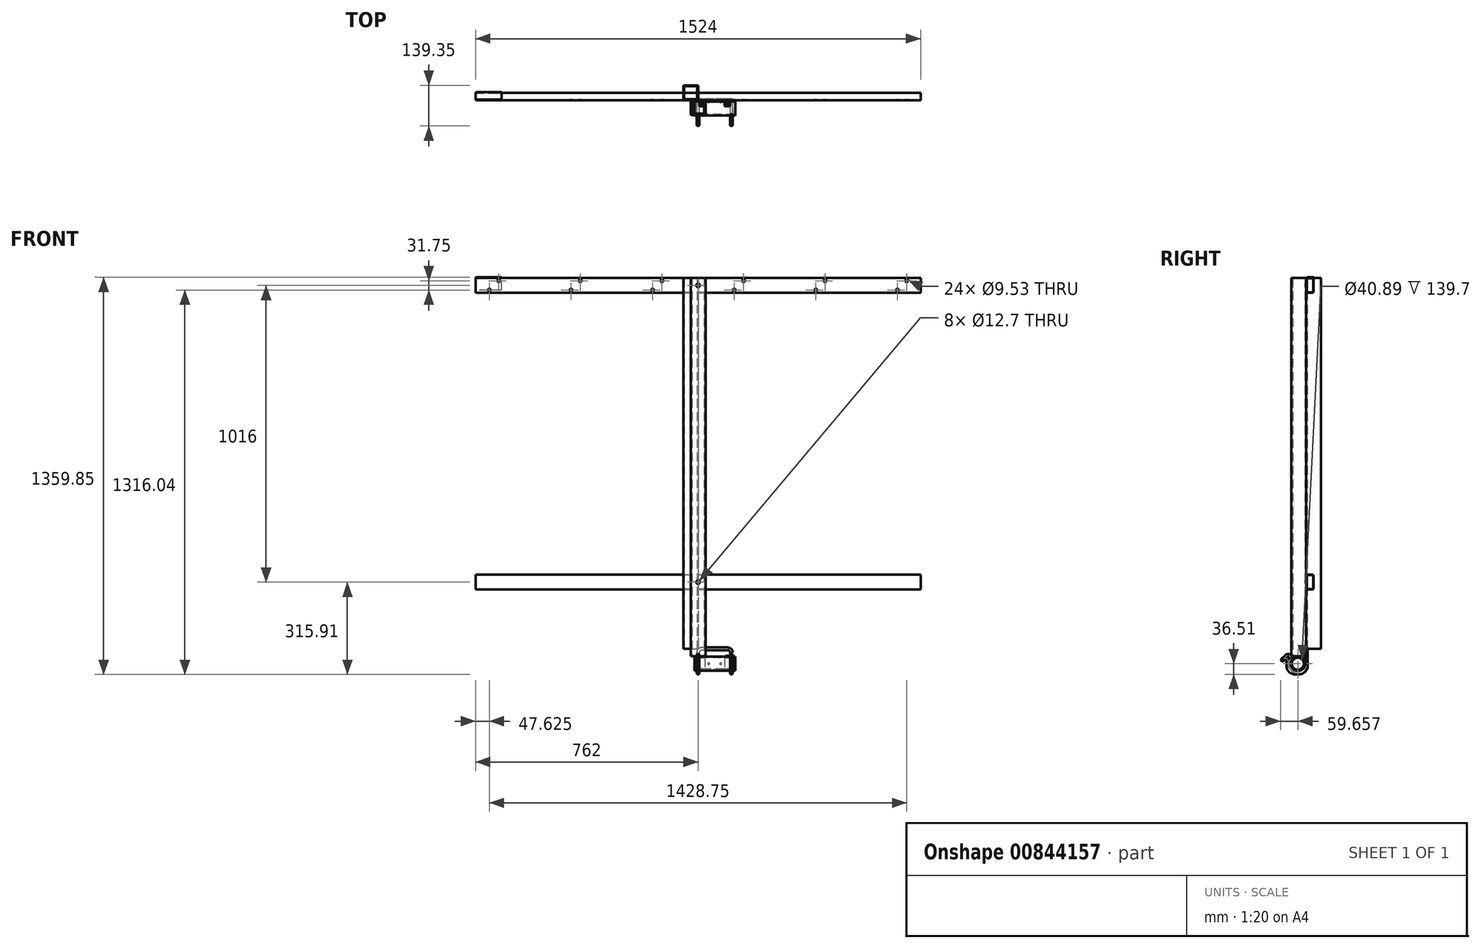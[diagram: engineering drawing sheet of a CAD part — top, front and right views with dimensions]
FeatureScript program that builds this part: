
annotation { "Feature Type Name" : "Feature", "Feature Type Description" : "" }
export const myFeature = defineFeature(function(context is Context, id is Id, definition is map)
    precondition{}
    {
        {
            var Q0;
            Q0=qCreatedBy(makeId("Top.planeOp"),FACE);
            cPlane(context, id + "F0", {"entities" : qUnion([Q0]), "cplaneType" : CPlaneType.OFFSET, "offset" : 457.2 * mm, "oppositeDirection" : true, "width" : 152.4 * mm, "height" : 152.4 * mm});
        }
        {
            var Q0;
            Q0=qCreatedBy(makeId("Front.planeOp"),FACE);
            var sketch = newSketch(context, id + "F1", { "sketchPlane" : qUnion([Q0])});
            skCircle(sketch, "E0.cCircle", {"center": v(0, 0) * mm, "radius": 25.4 * mm, "construction": true});
            skLineSegment(sketch, "E0.0", {"start": v(-25.4, -25.4) * mm, "end": v(-25.4, 25.4) * mm});
            skLineSegment(sketch, "E0.1", {"start": v(-25.4, 25.4) * mm, "end": v(25.4, 25.4) * mm});
            skLineSegment(sketch, "E0.2", {"start": v(25.4, 25.4) * mm, "end": v(25.4, -25.4) * mm});
            skLineSegment(sketch, "E0.3", {"start": v(25.4, -25.4) * mm, "end": v(-25.4, -25.4) * mm});
            skPoint(sketch, "E0.0.midPoint", {"position": v(-25.4, 0) * mm});
            skSolve(sketch);
        }
        {
            var Q0;
            Q0=qCreatedBy(makeId("Right.planeOp"),FACE);
            var sketch = newSketch(context, id + "F2", { "sketchPlane" : qUnion([Q0])});
            skCircle(sketch, "E1", {"center": v(-543.84, -137.57) * mm, "radius": 368.3 * mm, "construction": true});
            skLineSegment(sketch, "E2", {"start": v(-519.16, -505.04) * mm, "end": v(1678.67, -357.4) * mm, "construction": true});
            skCircle(sketch, "E3", {"center": v(613.45, -59.82) * mm, "radius": 368.3 * mm, "construction": true});
            skLineSegment(sketch, "E4", {"start": v(-327.65, 542.52) * mm, "end": v(-154.24, 174.4) * mm, "construction": true});
            skLineSegment(sketch, "E5", {"start": v(-543.84, -137.57) * mm, "end": v(16.21, -99.94) * mm, "construction": true});
            skLineSegment(sketch, "E6", {"start": v(16.21, -99.94) * mm, "end": v(324.48, 435.04) * mm, "construction": true});
            skLineSegment(sketch, "E7", {"start": v(280.4, 522.43) * mm, "end": v(566.34, -44.62) * mm, "construction": true});
            skLineSegment(sketch, "E8", {"start": v(-485.82, 531.9) * mm, "end": v(-227.77, 549.23) * mm, "construction": true});
            skCircle(sketch, "E9", {"center": v(613.45, -59.82) * mm, "radius": 101.6 * mm, "construction": true});
            skCircle(sketch, "E10", {"center": v(-543.84, -137.57) * mm, "radius": 88.9 * mm, "construction": true});
            skLineSegment(sketch, "E11", {"start": v(280.4, 522.43) * mm, "end": v(-543.84, -137.57) * mm, "construction": true});
            skLineSegment(sketch, "E12", {"start": v(-235.61, 347.14) * mm, "end": v(21.55, 315.16) * mm, "construction": true});
            skLineSegment(sketch, "E13", {"start": v(280.4, 522.43) * mm, "end": v(-659.31, 212.17) * mm, "construction": true});
            skSolve(sketch);
        }
        {
            var Q0;
            Q0=qCreatedBy(makeId("Front.planeOp"),FACE);
            var sketch = newSketch(context, id + "F3", { "sketchPlane" : qUnion([Q0])});
            skLineSegment(sketch, "E14.bottom", {"start": v(-762, 1270) * mm, "end": v(762, 1270) * mm});
            skLineSegment(sketch, "E14.top", {"start": v(-762, 1219.2) * mm, "end": v(762, 1219.2) * mm});
            skLineSegment(sketch, "E14.left", {"start": v(-762, 1270) * mm, "end": v(-762, 1219.2) * mm});
            skLineSegment(sketch, "E14.right", {"start": v(762, 1270) * mm, "end": v(762, 1219.2) * mm});
            skPoint(sketch, "E15", {"position": v(0, 1219.2) * mm});
            skLineSegment(sketch, "E16", {"start": v(-484.85, -460.8) * mm, "end": v(945.74, -460.8) * mm, "construction": true});
            skLineSegment(sketch, "E17", {"start": v(433.58, 979.68) * mm, "end": v(963.42, 1509.52) * mm, "construction": true});
            skPoint(sketch, "E18", {"position": v(698.5, 1244.6) * mm});
            skPoint(sketch, "E19", {"position": v(762, 1244.6) * mm});
            skLineSegment(sketch, "E20", {"start": v(0, 1219.2) * mm, "end": v(0, 0) * mm, "construction": true});
            skLineSegment(sketch, "E21.0", {"start": v(-762, 1260.47) * mm, "end": v(762, 1260.48) * mm, "construction": true});
            skLineSegment(sketch, "E22.0", {"start": v(-762, 1228.72) * mm, "end": v(762, 1228.73) * mm, "construction": true});
            skPoint(sketch, "E23", {"position": v(714.38, 1260.48) * mm});
            skPoint(sketch, "E24", {"position": v(682.63, 1228.73) * mm});
            skCircle(sketch, "E25", {"center": v(682.63, 1228.73) * mm, "radius": 4.76 * mm});
            skCircle(sketch, "E26", {"center": v(714.38, 1260.48) * mm, "radius": 4.76 * mm});
            skLineSegment(sketch, "E27.1.0.0", {"start": v(154.18, 979.68) * mm, "end": v(684.02, 1509.52) * mm, "construction": true});
            skLineSegment(sketch, "E27.2.0.0", {"start": v(-125.22, 979.68) * mm, "end": v(404.62, 1509.52) * mm, "construction": true});
            skLineSegment(sketch, "E27.3.0.0", {"start": v(-404.62, 979.68) * mm, "end": v(125.22, 1509.52) * mm, "construction": true});
            skLineSegment(sketch, "E27.4.0.0", {"start": v(-684.02, 979.68) * mm, "end": v(-154.18, 1509.52) * mm, "construction": true});
            skLineSegment(sketch, "E27.5.0.0", {"start": v(-963.42, 979.68) * mm, "end": v(-433.58, 1509.52) * mm, "construction": true});
            skLineSegment(sketch, "E27.direction1", {"start": v(433.58, 979.68) * mm, "end": v(154.18, 979.68) * mm, "construction": true});
            skLineSegment(sketch, "E28.bottom", {"start": v(-762, 203.2) * mm, "end": v(762, 203.2) * mm});
            skLineSegment(sketch, "E28.top", {"start": v(-762, 254) * mm, "end": v(762, 254) * mm});
            skLineSegment(sketch, "E28.left", {"start": v(-762, 203.2) * mm, "end": v(-762, 254) * mm});
            skLineSegment(sketch, "E28.right", {"start": v(762, 203.2) * mm, "end": v(762, 254) * mm});
            skLineSegment(sketch, "E29", {"start": v(762, 1244.6) * mm, "end": v(-762, 1244.6) * mm, "construction": true});
            skPoint(sketch, "E30", {"position": v(762, 228.6) * mm});
            skLineSegment(sketch, "E31", {"start": v(438.07, 1505.03) * mm, "end": v(698.5, 1244.6) * mm, "construction": true});
            skSolve(sketch);
        }
        {
            var Q0;
            Q0=sQuery(id+"F3.wireOp",EDGE,"E29");
            cPoint(context, id + "F4", {"entities" : qUnion([Q0]), "parameter" : 0.5});
        }
        {
            var Q0;
            Q0 = qCreatedBy(id + "F4" ,VERTEX);
            var Q1;
            Q1=sQuery(id+"F3.wireOp",EDGE,"E20");
            cPlane(context, id + "F5", {"entities" : qUnion([Q0, Q1]), "cplaneType" : CPlaneType.LINE_POINT, "offset" : 25.4 * mm, "width" : 152.4 * mm, "height" : 152.4 * mm});
        }
        {
            var Q0;
            Q0=qCreatedBy(makeId("Front.planeOp"),FACE);
            var sketch = newSketch(context, id + "F6", { "sketchPlane" : qUnion([Q0])});
            skLineSegment(sketch, "E32.bottom", {"start": v(-25.4, 1270) * mm, "end": v(25.4, 1270) * mm});
            skLineSegment(sketch, "E32.top", {"start": v(-25.4, 0) * mm, "end": v(25.4, 0) * mm});
            skLineSegment(sketch, "E32.left", {"start": v(-25.4, 1270) * mm, "end": v(-25.4, 0) * mm});
            skLineSegment(sketch, "E32.right", {"start": v(25.4, 1270) * mm, "end": v(25.4, 0) * mm});
            skPoint(sketch, "E33", {"position": v(0, 0) * mm});
            skLineSegment(sketch, "E34", {"start": v(301.3, 736.6) * mm, "end": v(-528.15, 736.6) * mm, "construction": true});
            skSolve(sketch);
        }
        {
            var Q0;
            Q0=qCreatedBy(makeId("Front.planeOp"),FACE);
            var sketch = newSketch(context, id + "F7", { "sketchPlane" : qUnion([Q0])});
            skLineSegment(sketch, "E35", {"start": v(381, 1244.6) * mm, "end": v(0, 863.6) * mm, "construction": true});
            skLineSegment(sketch, "E36", {"start": v(0, 482.6) * mm, "end": v(254, 228.6) * mm, "construction": true});
            skLineSegment(sketch, "E37", {"start": v(762, 228.6) * mm, "end": v(-497.78, 228.6) * mm, "construction": true});
            skSolve(sketch);
        }
        {
            var Q0;
            Q0=qCreatedBy(makeId("Front.planeOp"),FACE);
            var sketch = newSketch(context, id + "F8", { "sketchPlane" : qUnion([Q0])});
            skLineSegment(sketch, "E38.bottom", {"start": v(-25.4, 1270) * mm, "end": v(25.4, 1270) * mm});
            skLineSegment(sketch, "E38.top", {"start": v(-25.4, -25.4) * mm, "end": v(25.4, -25.4) * mm});
            skLineSegment(sketch, "E38.left", {"start": v(-25.4, 1270) * mm, "end": v(-25.4, -25.4) * mm});
            skLineSegment(sketch, "E38.right", {"start": v(25.4, 1270) * mm, "end": v(25.4, -25.4) * mm});
            skSolve(sketch);
        }
        {
            var Q0;
            Q0 = qSketchRegion(id + "F8", true);
            extrude(context, id + "F9", {"entities" : qUnion([Q0]), "depth" : 50.8 * mm, "offsetDistance" : 25.4 * mm});
        }
        {
            var Q0;
            Q0=makeQuery(id+"F9.opExtrude","SWEPT_FACE",FACE,{"disambiguationData":[OSD([sQuery(id+"F8.wireOp",EDGE,"E38.bottom")])]});
            var Q1;
            Q1=makeQuery(id+"F9.opExtrude","SWEPT_FACE",FACE,{"disambiguationData":[OSD([sQuery(id+"F8.wireOp",EDGE,"E38.top")])]});
            shell(context, id + "F10", {"entities" : qUnion([Q0, Q1]), "thickness" : 4.78 * mm});
        }
        {
            var Q0;
            Q0=qCreatedBy(makeId("Front.planeOp"),FACE);
            var sketch = newSketch(context, id + "F11", { "sketchPlane" : qUnion([Q0])});
            skLineSegment(sketch, "E39.bottom", {"start": v(-762, 1270) * mm, "end": v(762, 1270) * mm});
            skLineSegment(sketch, "E39.top", {"start": v(-762, 1219.2) * mm, "end": v(762, 1219.2) * mm});
            skLineSegment(sketch, "E39.left", {"start": v(-762, 1270) * mm, "end": v(-762, 1219.2) * mm});
            skLineSegment(sketch, "E39.right", {"start": v(762, 1270) * mm, "end": v(762, 1219.2) * mm});
            skSolve(sketch);
        }
        {
            var Q0;
            Q0 = qSketchRegion(id + "F11", true);
            extrude(context, id + "F12", {"entities" : qUnion([Q0]), "oppositeDirection" : true, "depth" : 25.4 * mm, "offsetDistance" : 25.4 * mm});
        }
        {
            var Q0;
            Q0=makeQuery(id+"F12.opExtrude","CAP_EDGE",EDGE,{"disambiguationData":[OSD([sQuery(id+"F11.wireOp",EDGE,"E39.bottom")])],"isStart":true});
            var Q1;
            Q1=makeQuery(id+"F12.opExtrude","CAP_EDGE",EDGE,{"disambiguationData":[OSD([sQuery(id+"F11.wireOp",EDGE,"E39.top")])],"isStart":true});
            var Q2;
            Q2=makeQuery(id+"F12.opExtrude","CAP_EDGE",EDGE,{"disambiguationData":[OSD([sQuery(id+"F11.wireOp",EDGE,"E39.bottom")])],"isStart":false});
            var Q3;
            Q3=makeQuery(id+"F12.opExtrude","CAP_EDGE",EDGE,{"disambiguationData":[OSD([sQuery(id+"F11.wireOp",EDGE,"E39.top")])],"isStart":false});
            fillet(context, id + "F13", {"entities" : qUnion([Q0, Q1, Q2, Q3]), "radius" : 5.08 * mm, "tangentPropagation" : true, "allowEdgeOverflow" : false});
        }
        {
            var Q0;
            Q0=makeQuery(id+"F12.opExtrude","SWEPT_FACE",FACE,{"disambiguationData":[OSD([sQuery(id+"F11.wireOp",EDGE,"E39.right")])]});
            var Q1;
            Q1=makeQuery(id+"F12.opExtrude","SWEPT_FACE",FACE,{"disambiguationData":[OSD([sQuery(id+"F11.wireOp",EDGE,"E39.left")])]});
            shell(context, id + "F14", {"entities" : qUnion([Q0, Q1]), "thickness" : 1.6 * mm});
        }
        {
            var Q0;
            Q0=makeQuery(id+"F3.imprint","IMPRINT",FACE,{"disambiguationData":[TD([[makeQuery(id+"F3.imprint","IMPRINT",EDGE,{"derivedFrom":sQuery(id+"F3.wireOp",EDGE,"E14.bottom")}),-1.0]])]});
            var sketch = newSketch(context, id + "F15", { "sketchPlane" : qUnion([Q0])});
            skCircle(sketch, "E40", {"center": v(714.38, 1260.48) * mm, "radius": 4.76 * mm});
            skCircle(sketch, "E41", {"center": v(682.63, 1228.73) * mm, "radius": 4.76 * mm});
            skCircle(sketch, "E42.1.0.0", {"center": v(434.98, 1260.48) * mm, "radius": 4.76 * mm});
            skCircle(sketch, "E42.1.0.1", {"center": v(403.23, 1228.73) * mm, "radius": 4.76 * mm});
            skCircle(sketch, "E42.2.0.0", {"center": v(155.58, 1260.48) * mm, "radius": 4.76 * mm});
            skCircle(sketch, "E42.2.0.1", {"center": v(123.83, 1228.73) * mm, "radius": 4.76 * mm});
            skCircle(sketch, "E42.3.0.0", {"center": v(-123.82, 1260.48) * mm, "radius": 4.76 * mm});
            skCircle(sketch, "E42.3.0.1", {"center": v(-155.57, 1228.73) * mm, "radius": 4.76 * mm});
            skCircle(sketch, "E42.4.0.0", {"center": v(-403.22, 1260.47) * mm, "radius": 4.76 * mm});
            skCircle(sketch, "E42.4.0.1", {"center": v(-434.97, 1228.73) * mm, "radius": 4.76 * mm});
            skCircle(sketch, "E42.5.0.0", {"center": v(-682.62, 1260.47) * mm, "radius": 4.76 * mm});
            skCircle(sketch, "E42.5.0.1", {"center": v(-714.37, 1228.73) * mm, "radius": 4.76 * mm});
            skLineSegment(sketch, "E42.direction1", {"start": v(714.38, 1260.48) * mm, "end": v(434.98, 1260.48) * mm, "construction": true});
            skSolve(sketch);
        }
        {
            var Q0;
            Q0 = qSketchRegion(id + "F15", true);
            extrude(context, id + "F16", {"entities" : qUnion([Q0]), "operationType" : NewBodyOperationType.REMOVE, "oppositeDirection" : true, "depth" : 25.4 * mm, "offsetDistance" : 25.4 * mm});
        }
        {
            var Q0;
            Q0=qCreatedBy(makeId("Front.planeOp"),FACE);
            var sketch = newSketch(context, id + "F17", { "sketchPlane" : qUnion([Q0])});
            skLineSegment(sketch, "E43.bottom", {"start": v(-762, 254) * mm, "end": v(762, 254) * mm});
            skLineSegment(sketch, "E43.top", {"start": v(-762, 203.2) * mm, "end": v(762, 203.2) * mm});
            skLineSegment(sketch, "E43.left", {"start": v(-762, 254) * mm, "end": v(-762, 203.2) * mm});
            skLineSegment(sketch, "E43.right", {"start": v(762, 254) * mm, "end": v(762, 203.2) * mm});
            skSolve(sketch);
        }
        {
            var Q0;
            Q0 = qSketchRegion(id + "F17", true);
            extrude(context, id + "F18", {"entities" : qUnion([Q0]), "oppositeDirection" : true, "depth" : 25.4 * mm, "offsetDistance" : 25.4 * mm});
        }
        {
            var Q0;
            Q0=makeQuery(id+"F18.opExtrude","CAP_EDGE",EDGE,{"disambiguationData":[OSD([sQuery(id+"F17.wireOp",EDGE,"E43.bottom")])],"isStart":true});
            var Q1;
            Q1=makeQuery(id+"F18.opExtrude","CAP_EDGE",EDGE,{"disambiguationData":[OSD([sQuery(id+"F17.wireOp",EDGE,"E43.bottom")])],"isStart":false});
            var Q2;
            Q2=makeQuery(id+"F18.opExtrude","CAP_EDGE",EDGE,{"disambiguationData":[OSD([sQuery(id+"F17.wireOp",EDGE,"E43.top")])],"isStart":true});
            var Q3;
            Q3=makeQuery(id+"F18.opExtrude","CAP_EDGE",EDGE,{"disambiguationData":[OSD([sQuery(id+"F17.wireOp",EDGE,"E43.top")])],"isStart":false});
            fillet(context, id + "F19", {"entities" : qUnion([Q0, Q1, Q2, Q3]), "radius" : 5.08 * mm, "tangentPropagation" : true, "allowEdgeOverflow" : false});
        }
        {
            var Q0;
            Q0=makeQuery(id+"F18.opExtrude","SWEPT_FACE",FACE,{"disambiguationData":[OSD([sQuery(id+"F17.wireOp",EDGE,"E43.right")])]});
            var Q1;
            Q1=makeQuery(id+"F18.opExtrude","SWEPT_FACE",FACE,{"disambiguationData":[OSD([sQuery(id+"F17.wireOp",EDGE,"E43.left")])]});
            shell(context, id + "F20", {"entities" : qUnion([Q0, Q1]), "thickness" : 1.6 * mm});
        }
        {
            var Q0;
            Q0=makeQuery(id+"F12.opExtrude","SWEPT_FACE",FACE,{"disambiguationData":[OSD([sQuery(id+"F11.wireOp",EDGE,"E39.left")])]});
            var sketch = newSketch(context, id + "F21", { "sketchPlane" : qUnion([Q0])});
            skLineSegment(sketch, "E44", {"start": v(-2.54, 1270) * mm, "end": v(-22.86, 1270) * mm});
            skLineSegment(sketch, "E45", {"start": v(-25.4, 1267.46) * mm, "end": v(-25.4, 1228.09) * mm});
            skLineSegment(sketch, "E46", {"start": v(-25.4, 1228.09) * mm, "end": v(-27.94, 1228.09) * mm});
            skLineSegment(sketch, "E47", {"start": v(-27.94, 1228.09) * mm, "end": v(-27.94, 1267.46) * mm});
            skLineSegment(sketch, "E48", {"start": v(-22.86, 1272.54) * mm, "end": v(-2.54, 1272.54) * mm});
            skLineSegment(sketch, "E49", {"start": v(-2.54, 1272.54) * mm, "end": v(-2.54, 1270) * mm});
            skPoint(sketch, "E50.visualSharp", {"position": v(-25.4, 1270) * mm});
            skArc(sketch, "E50.filletArc", {"start": v(-22.86, 1270) * mm, "mid": v(-24.66, 1269.26) * mm, "end": v(-25.4, 1267.46) * mm});
            skPoint(sketch, "E51.visualSharp", {"position": v(-27.94, 1272.54) * mm});
            skArc(sketch, "E51.filletArc", {"start": v(-22.86, 1272.54) * mm, "mid": v(-26.45, 1271.05) * mm, "end": v(-27.94, 1267.46) * mm});
            skSolve(sketch);
        }
        {
            var Q0;
            Q0 = qSketchRegion(id + "F21", true);
            extrude(context, id + "F22", {"entities" : qUnion([Q0]), "oppositeDirection" : true, "depth" : 88.9 * mm, "offsetDistance" : 25.4 * mm});
        }
        {
            var Q0;
            Q0=makeQuery(id+"F22.opExtrude","CAP_FACE",FACE,{"disambiguationData":[OSD([sQuery(id+"F21.wireOp",EDGE,"E44"),sQuery(id+"F21.wireOp",EDGE,"E45"),sQuery(id+"F21.wireOp",EDGE,"E46"),sQuery(id+"F21.wireOp",EDGE,"E47"),sQuery(id+"F21.wireOp",EDGE,"E48"),sQuery(id+"F21.wireOp",EDGE,"E49"),sQuery(id+"F21.wireOp",EDGE,"E50.filletArc"),sQuery(id+"F21.wireOp",EDGE,"E51.filletArc")])],"isStart":true});
            cPlane(context, id + "F23", {"entities" : qUnion([Q0]), "cplaneType" : CPlaneType.OFFSET, "offset" : 6.35 * mm, "oppositeDirection" : true, "width" : 152.4 * mm, "height" : 152.4 * mm});
        }
        {
            var Q0;
            Q0=qCreatedBy(id+"F23.planeOp",FACE);
            var sketch = newSketch(context, id + "F24", { "sketchPlane" : qUnion([Q0])});
            skLineSegment(sketch, "E52", {"start": v(-32.7, 1270) * mm, "end": v(-32.7, 1244.6) * mm});
            skArc(sketch, "E53", {"start": v(-96.2, 1244.6) * mm, "mid": v(-64.45, 1212.85) * mm, "end": v(-32.7, 1244.6) * mm});
            skLineSegment(sketch, "E54", {"start": v(-96.2, 1244.6) * mm, "end": v(-96.2, 1262.1) * mm});
            skLineSegment(sketch, "E55", {"start": v(-101.78, 1275.58) * mm, "end": v(-105.18, 1278.98) * mm});
            skPoint(sketch, "E56.visualSharp", {"position": v(-96.2, 1270) * mm});
            skArc(sketch, "E56.filletArc", {"start": v(-96.2, 1262.1) * mm, "mid": v(-97.65, 1269.4) * mm, "end": v(-101.78, 1275.58) * mm});
            skSolve(sketch);
        }
        {
            var Q0;
            Q0=makeQuery(id+"F22.opExtrude","CAP_FACE",FACE,{"disambiguationData":[OSD([sQuery(id+"F21.wireOp",EDGE,"E44"),sQuery(id+"F21.wireOp",EDGE,"E45"),sQuery(id+"F21.wireOp",EDGE,"E46"),sQuery(id+"F21.wireOp",EDGE,"E47"),sQuery(id+"F21.wireOp",EDGE,"E48"),sQuery(id+"F21.wireOp",EDGE,"E49"),sQuery(id+"F21.wireOp",EDGE,"E50.filletArc"),sQuery(id+"F21.wireOp",EDGE,"E51.filletArc")])],"isStart":false});
            cPlane(context, id + "F25", {"entities" : qUnion([Q0]), "cplaneType" : CPlaneType.OFFSET, "offset" : 6.35 * mm, "oppositeDirection" : true, "width" : 152.4 * mm, "height" : 152.4 * mm});
        }
        {
            var Q0;
            Q0=qCreatedBy(id+"F25.planeOp",FACE);
            var sketch = newSketch(context, id + "F26", { "sketchPlane" : qUnion([Q0])});
            skLineSegment(sketch, "E57", {"start": v(32.7, 1270) * mm, "end": v(32.7, 1168.4) * mm});
            skLineSegment(sketch, "E58", {"start": v(96.2, 1168.4) * mm, "end": v(96.2, 1185.9) * mm});
            skLineSegment(sketch, "E59", {"start": v(101.78, 1199.38) * mm, "end": v(114.16, 1211.76) * mm});
            skArc(sketch, "E60", {"start": v(32.7, 1168.4) * mm, "mid": v(64.45, 1136.65) * mm, "end": v(96.2, 1168.4) * mm});
            skPoint(sketch, "E61.visualSharp", {"position": v(96.2, 1193.8) * mm});
            skArc(sketch, "E61.filletArc", {"start": v(101.78, 1199.38) * mm, "mid": v(97.65, 1193.2) * mm, "end": v(96.2, 1185.9) * mm});
            skSolve(sketch);
        }
        {
            var Q0;
            Q0=sQuery(id+"F26.wireOp",VERTEX,"E57.start");
            var Q1;
            Q1=sQuery(id+"F26.wireOp",EDGE,"E57");
            cPlane(context, id + "F27", {"entities" : qUnion([Q0, Q1]), "cplaneType" : CPlaneType.LINE_POINT, "offset" : 25.4 * mm, "width" : 152.4 * mm, "height" : 152.4 * mm});
        }
        {
            var Q0;
            Q0=qCreatedBy(id+"F27.planeOp",FACE);
            var sketch = newSketch(context, id + "F28", { "sketchPlane" : qUnion([Q0])});
            skCircle(sketch, "E62", {"center": v(-679.45, -32.7) * mm, "radius": 4.76 * mm});
            skSolve(sketch);
        }
        {
            var Q0;
            Q0=makeQuery(id+"F28.imprint","IMPRINT",FACE,{"disambiguationData":[TD([[makeQuery(id+"F28.imprint","IMPRINT",EDGE,{"derivedFrom":sQuery(id+"F28.wireOp",EDGE,"E62")}),1.0]])]});
            var Q1;
            Q1 = qConstructionFilter(qBodyType(qCreatedBy(id + "F26" ,EDGE), BodyType.WIRE), ConstructionObject.NO);
            sweep(context, id + "F29", {"profiles" : qUnion([Q0]), "path" : qUnion([Q1])});
        }
        {
            var Q0;
            Q0=qCreatedBy(id+"F27.planeOp",FACE);
            var sketch = newSketch(context, id + "F30", { "sketchPlane" : qUnion([Q0])});
            skCircle(sketch, "E63", {"center": v(-755.65, -32.7) * mm, "radius": 4.76 * mm});
            skSolve(sketch);
        }
        {
            var Q0;
            Q0=makeQuery(id+"F30.imprint","IMPRINT",FACE,{"disambiguationData":[TD([[makeQuery(id+"F30.imprint","IMPRINT",EDGE,{"derivedFrom":sQuery(id+"F30.wireOp",EDGE,"E63")}),1.0]])]});
            var Q1;
            Q1=sQuery(id+"F30.wireOp",EDGE,"E63");
            var Q2;
            Q2 = qConstructionFilter(qBodyType(qCreatedBy(id + "F24" ,EDGE), BodyType.WIRE), ConstructionObject.NO);
            sweep(context, id + "F31", {"profiles" : qUnion([Q0]), "surfaceProfiles" : qUnion([Q1]), "path" : qUnion([Q2])});
        }
        {
            var Q0;
            Q0=sQuery(id+"F24.wireOp",VERTEX,"E53.center");
            var Q1;
            Q1=makeQuery(id+"F22.opExtrude","CAP_EDGE",EDGE,{"disambiguationData":[OSD([sQuery(id+"F21.wireOp",EDGE,"E48")])],"isStart":true});
            cPlane(context, id + "F32", {"entities" : qUnion([Q0, Q1]), "cplaneType" : CPlaneType.LINE_POINT, "offset" : 25.4 * mm, "oppositeDirection" : true, "width" : 152.4 * mm, "height" : 152.4 * mm});
        }
        {
            var Q0;
            Q0=qCreatedBy(id+"F25.planeOp",FACE);
            var sketch = newSketch(context, id + "F33", { "sketchPlane" : qUnion([Q0])});
            skLineSegment(sketch, "E64", {"start": v(32.7, 1270) * mm, "end": v(32.7, 1219.2) * mm});
            skLineSegment(sketch, "E65", {"start": v(96.2, 1162.05) * mm, "end": v(96.2, 1187.45) * mm});
            skArc(sketch, "E66", {"start": v(46, 1156.54) * mm, "mid": v(73.57, 1136.8) * mm, "end": v(96.2, 1162.05) * mm});
            skArc(sketch, "E67", {"start": v(96.2, 1187.45) * mm, "mid": v(104.04, 1199.18) * mm, "end": v(117.88, 1196.43) * mm});
            skPoint(sketch, "E68.orphan", {"position": v(32.7, 1162.05) * mm});
            skPoint(sketch, "E69.visualSharp", {"position": v(32.7, 1181.1) * mm});
            skArc(sketch, "E69.filletArc", {"start": v(32.7, 1219.2) * mm, "mid": v(32.85, 1216.43) * mm, "end": v(33.3, 1213.69) * mm});
            skPoint(sketch, "E70.visualSharp", {"position": v(51.75, 1187.45) * mm});
            skCircle(sketch, "E71", {"center": v(70.8, 1162.05) * mm, "radius": 15.88 * mm, "construction": true});
            skLineSegment(sketch, "E72", {"start": v(55.67, 1136.65) * mm, "end": v(70.8, 1136.65) * mm, "construction": true});
            skPoint(sketch, "E72.startSnap0", {"position": v(70.8, 1136.65) * mm});
            skLineSegment(sketch, "E73", {"start": v(108.9, 1187.45) * mm, "end": v(117.88, 1196.43) * mm, "construction": true});
            skLineSegment(sketch, "E74", {"start": v(46, 1156.54) * mm, "end": v(33.3, 1213.69) * mm});
            skPoint(sketch, "E75.orphan", {"position": v(45.4, 1162.05) * mm});
            skSolve(sketch);
        }
        {
            var Q0;
            Q0 = qSketchRegion(id + "F28", true);
            var Q1;
            Q1 = qConstructionFilter(qBodyType(qCreatedBy(id + "F33" ,EDGE), BodyType.WIRE), ConstructionObject.NO);
            sweep(context, id + "F34", {"operationType" : NewBodyOperationType.ADD, "profiles" : qUnion([Q0]), "path" : qUnion([Q1])});
        }
        {
            var Q0;
            Q0=qCreatedBy(id+"F23.planeOp",FACE);
            var sketch = newSketch(context, id + "F35", { "sketchPlane" : qUnion([Q0])});
            skLineSegment(sketch, "E76", {"start": v(-32.7, 1270) * mm, "end": v(-32.7, 1244.6) * mm});
            skLineSegment(sketch, "E77", {"start": v(-36.73, 1235.32) * mm, "end": v(-53.46, 1219.69) * mm});
            skLineSegment(sketch, "E78", {"start": v(-96.2, 1238.25) * mm, "end": v(-96.2, 1263.65) * mm});
            skArc(sketch, "E79", {"start": v(-96.2, 1238.25) * mm, "mid": v(-80.92, 1214.95) * mm, "end": v(-53.46, 1219.69) * mm});
            skPoint(sketch, "E80.visualSharp", {"position": v(-32.7, 1239.08) * mm});
            skArc(sketch, "E80.filletArc", {"start": v(-36.73, 1235.32) * mm, "mid": v(-33.75, 1239.54) * mm, "end": v(-32.7, 1244.6) * mm});
            skLineSegment(sketch, "E81", {"start": v(-70.8, 1212.85) * mm, "end": v(11.7, 1212.85) * mm, "construction": true});
            skArc(sketch, "E82", {"start": v(-96.2, 1263.65) * mm, "mid": v(-104.04, 1275.38) * mm, "end": v(-117.88, 1272.63) * mm});
            skLineSegment(sketch, "E83", {"start": v(-108.9, 1263.65) * mm, "end": v(-117.88, 1272.63) * mm, "construction": true});
            skSolve(sketch);
        }
        {
            var Q0;
            Q0 = qSketchRegion(id + "F30", true);
            var Q1;
            Q1 = qConstructionFilter(qBodyType(qCreatedBy(id + "F35" ,EDGE), BodyType.WIRE), ConstructionObject.NO);
            sweep(context, id + "F36", {"operationType" : NewBodyOperationType.ADD, "profiles" : qUnion([Q0]), "path" : qUnion([Q1])});
        }
        {
            var Q0;
            Q0=makeQuery(id+"F34.opSweep","CAP_EDGE",EDGE,{"disambiguationData":[OSD([sQuery(id+"F28.wireOp",EDGE,"E62"),sQuery(id+"F33.wireOp",VERTEX,"E67.end")])],"isStart":false});
            var Q1;
            Q1=makeQuery(id+"F36.opSweep","CAP_EDGE",EDGE,{"disambiguationData":[OSD([sQuery(id+"F30.wireOp",EDGE,"E63"),sQuery(id+"F35.wireOp",VERTEX,"E82.end")])],"isStart":false});
            var Q2;
            Q2=makeQuery(id+"F36.opSweep","CAP_EDGE",EDGE,{"disambiguationData":[OSD([sQuery(id+"F30.wireOp",EDGE,"E63"),sQuery(id+"F35.wireOp",VERTEX,"E76.start")])],"isStart":true});
            var Q3;
            Q3=makeQuery(id+"F34.opSweep","CAP_EDGE",EDGE,{"disambiguationData":[OSD([sQuery(id+"F28.wireOp",EDGE,"E62"),sQuery(id+"F33.wireOp",VERTEX,"E64.start")])],"isStart":true});
            fillet(context, id + "F37", {"entities" : qUnion([Q0, Q1, Q2, Q3]), "radius" : 2.54 * mm, "tangentPropagation" : true, "allowEdgeOverflow" : false});
        }
        {
            var Q0;
            Q0=makeQuery(id+"F12.opExtrude","CAP_FACE",FACE,{"disambiguationData":[OSD([sQuery(id+"F11.wireOp",EDGE,"E39.bottom"),sQuery(id+"F11.wireOp",EDGE,"E39.top"),sQuery(id+"F11.wireOp",EDGE,"E39.left"),sQuery(id+"F11.wireOp",EDGE,"E39.right")])],"isStart":false});
            var sketch = newSketch(context, id + "F38", { "sketchPlane" : qUnion([Q0])});
            skCircle(sketch, "E84", {"center": v(0, 1244.6) * mm, "radius": 6.35 * mm});
            skSolve(sketch);
        }
        {
            var Q0;
            Q0 = qSketchRegion(id + "F38", true);
            extrude(context, id + "F39", {"entities" : qUnion([Q0]), "operationType" : NewBodyOperationType.REMOVE, "endBound" : BoundingType.THROUGH_ALL, "oppositeDirection" : true, "depth" : 25.4 * mm, "offsetDistance" : 25.4 * mm});
        }
        {
            var Q0;
            Q0=makeQuery(id+"F18.opExtrude","CAP_FACE",FACE,{"disambiguationData":[OSD([sQuery(id+"F17.wireOp",EDGE,"E43.bottom"),sQuery(id+"F17.wireOp",EDGE,"E43.top"),sQuery(id+"F17.wireOp",EDGE,"E43.left"),sQuery(id+"F17.wireOp",EDGE,"E43.right")])],"isStart":false});
            var sketch = newSketch(context, id + "F40", { "sketchPlane" : qUnion([Q0])});
            skCircle(sketch, "E85", {"center": v(0, 228.6) * mm, "radius": 6.35 * mm});
            skSolve(sketch);
        }
        {
            var Q0;
            Q0 = qSketchRegion(id + "F40", true);
            extrude(context, id + "F41", {"entities" : qUnion([Q0]), "operationType" : NewBodyOperationType.REMOVE, "endBound" : BoundingType.THROUGH_ALL, "oppositeDirection" : true, "depth" : 25.4 * mm, "offsetDistance" : 25.4 * mm});
        }
        {
            var Q0;
            Q0=qCreatedBy(makeId("Front.planeOp"),FACE);
            var sketch = newSketch(context, id + "F42", { "sketchPlane" : qUnion([Q0])});
            skLineSegment(sketch, "E86", {"start": v(12.7, 0) * mm, "end": v(101.6, 0) * mm});
            skLineSegment(sketch, "E87", {"start": v(0, -12.7) * mm, "end": v(0, -50.8) * mm});
            skLineSegment(sketch, "E88", {"start": v(114.3, -12.7) * mm, "end": v(114.3, -50.8) * mm});
            skPoint(sketch, "E89.visualSharp", {"position": v(0, 0) * mm});
            skArc(sketch, "E89.filletArc", {"start": v(12.7, 0) * mm, "mid": v(3.72, -3.72) * mm, "end": v(0, -12.7) * mm});
            skPoint(sketch, "E90.visualSharp", {"position": v(114.3, 0) * mm});
            skArc(sketch, "E90.filletArc", {"start": v(114.3, -12.7) * mm, "mid": v(110.58, -3.72) * mm, "end": v(101.6, 0) * mm});
            skSolve(sketch);
        }
        {
            var Q0;
            Q0=qCreatedBy(makeId("Right.planeOp"),FACE);
            var sketch = newSketch(context, id + "F43", { "sketchPlane" : qUnion([Q0])});
            skArc(sketch, "E91", {"start": v(-53.91, -36.35) * mm, "mid": v(-36.37, -78.7) * mm, "end": v(0, -50.8) * mm});
            skLineSegment(sketch, "E92", {"start": v(-28.9, -50.8) * mm, "end": v(-53.91, -36.35) * mm, "construction": true});
            skLineSegment(sketch, "E93", {"start": v(-28.9, -50.8) * mm, "end": v(0, -50.8) * mm, "construction": true});
            skArc(sketch, "E94", {"start": v(-53.91, -36.35) * mm, "mid": v(-57.4, -23.34) * mm, "end": v(-70.41, -26.83) * mm});
            skLineSegment(sketch, "E95", {"start": v(-70.41, -26.83) * mm, "end": v(-75.17, -35.08) * mm});
            skSolve(sketch);
        }
        {
            var Q0;
            Q0=qCreatedBy(makeId("Right.planeOp"),FACE);
            var Q1;
            Q1=sQuery(id+"F42.wireOp",VERTEX,"E88.end");
            cPlane(context, id + "F44", {"entities" : qUnion([Q0, Q1]), "cplaneType" : CPlaneType.PLANE_POINT, "offset" : 25.4 * mm, "width" : 152.4 * mm, "height" : 152.4 * mm});
        }
        {
            var Q0;
            Q0=qCreatedBy(id+"F44.planeOp",FACE);
            var sketch = newSketch(context, id + "F45", { "sketchPlane" : qUnion([Q0])});
            skArc(sketch, "E96", {"start": v(-53.91, -36.35) * mm, "mid": v(-36.37, -78.7) * mm, "end": v(0, -50.8) * mm});
            skArc(sketch, "E97", {"start": v(-53.91, -36.35) * mm, "mid": v(-57.4, -23.34) * mm, "end": v(-70.41, -26.83) * mm});
            skLineSegment(sketch, "E98", {"start": v(-28.9, -50.8) * mm, "end": v(-53.91, -36.35) * mm, "construction": true});
            skLineSegment(sketch, "E99", {"start": v(-28.9, -50.8) * mm, "end": v(0, -50.8) * mm, "construction": true});
            skLineSegment(sketch, "E100", {"start": v(-70.41, -26.83) * mm, "end": v(-76.76, -37.83) * mm});
            skSolve(sketch);
        }
        {
            var Q0;
            Q0=sQuery(id+"F43.wireOp",VERTEX,"E95.end");
            var Q1;
            Q1=sQuery(id+"F43.wireOp",EDGE,"E95");
            cPlane(context, id + "F46", {"entities" : qUnion([Q0, Q1]), "cplaneType" : CPlaneType.LINE_POINT, "offset" : 25.4 * mm, "width" : 152.4 * mm, "height" : 152.4 * mm});
        }
        {
            var Q0;
            Q0=qCreatedBy(id+"F46.planeOp",FACE);
            var sketch = newSketch(context, id + "F47", { "sketchPlane" : qUnion([Q0])});
            skCircle(sketch, "E101", {"center": v(0, 47.56) * mm, "radius": 4.76 * mm});
            skSolve(sketch);
        }
        {
            var Q0;
            Q0=makeQuery(id+"F47.imprint","IMPRINT",FACE,{"disambiguationData":[TD([[makeQuery(id+"F47.imprint","IMPRINT",EDGE,{"derivedFrom":sQuery(id+"F47.wireOp",EDGE,"E101")}),1.0]])]});
            var Q1;
            Q1=sQuery(id+"F47.wireOp",EDGE,"E101");
            var Q2;
            Q2=sQuery(id+"F43.wireOp",EDGE,"E95");
            var Q3;
            Q3=sQuery(id+"F43.wireOp",EDGE,"E94");
            var Q4;
            Q4=sQuery(id+"F43.wireOp",EDGE,"E91");
            var Q5;
            Q5=sQuery(id+"F42.wireOp",EDGE,"E87");
            var Q6;
            Q6=sQuery(id+"F42.wireOp",EDGE,"E89.filletArc");
            var Q7;
            Q7=sQuery(id+"F42.wireOp",EDGE,"E86");
            var Q8;
            Q8=sQuery(id+"F42.wireOp",EDGE,"E90.filletArc");
            var Q9;
            Q9=sQuery(id+"F42.wireOp",EDGE,"E88");
            var Q10;
            Q10=sQuery(id+"F45.wireOp",EDGE,"E96");
            var Q11;
            Q11=sQuery(id+"F45.wireOp",EDGE,"E97");
            var Q12;
            Q12=sQuery(id+"F45.wireOp",EDGE,"E100");
            sweep(context, id + "F48", {"profiles" : qUnion([Q0]), "surfaceProfiles" : qUnion([Q1]), "path" : qUnion([Q2, Q3, Q4, Q5, Q6, Q7, Q8, Q9, Q10, Q11, Q12])});
        }
        {
            var Q0;
            Q0=qCreatedBy(id+"F44.planeOp",FACE);
            var sketch = newSketch(context, id + "F49", { "sketchPlane" : qUnion([Q0])});
            skLineSegment(sketch, "E102", {"start": v(0, -50.8) * mm, "end": v(0, -57.15) * mm});
            skLineSegment(sketch, "E103", {"start": v(-25.4, -82.55) * mm, "end": v(-38.1, -82.55) * mm});
            skLineSegment(sketch, "E104", {"start": v(-63.5, -57.15) * mm, "end": v(-63.5, -39.69) * mm});
            skLineSegment(sketch, "E105", {"start": v(-71.44, -31.75) * mm, "end": v(-72.91, -31.75) * mm});
            skLineSegment(sketch, "E106", {"start": v(-78.52, -34.07) * mm, "end": v(-85.18, -40.73) * mm});
            skPoint(sketch, "E107.visualSharp", {"position": v(-76.2, -31.75) * mm});
            skArc(sketch, "E107.filletArc", {"start": v(-72.91, -31.75) * mm, "mid": v(-75.95, -32.35) * mm, "end": v(-78.52, -34.07) * mm});
            skPoint(sketch, "E108.visualSharp", {"position": v(-63.5, -31.75) * mm});
            skArc(sketch, "E108.filletArc", {"start": v(-63.5, -39.69) * mm, "mid": v(-65.82, -34.07) * mm, "end": v(-71.44, -31.75) * mm});
            skPoint(sketch, "E109.visualSharp", {"position": v(-63.5, -82.55) * mm});
            skArc(sketch, "E109.filletArc", {"start": v(-63.5, -57.15) * mm, "mid": v(-56.06, -75.11) * mm, "end": v(-38.1, -82.55) * mm});
            skPoint(sketch, "E110.visualSharp", {"position": v(0, -82.55) * mm});
            skArc(sketch, "E110.filletArc", {"start": v(-25.4, -82.55) * mm, "mid": v(-7.44, -75.11) * mm, "end": v(0, -57.15) * mm});
            skSolve(sketch);
        }
        {
            var Q0;
            Q0=qCreatedBy(makeId("Right.planeOp"),FACE);
            var sketch = newSketch(context, id + "F50", { "sketchPlane" : qUnion([Q0])});
            skLineSegment(sketch, "E111", {"start": v(0, -50.8) * mm, "end": v(0, -57.15) * mm});
            skLineSegment(sketch, "E112", {"start": v(-25.4, -82.55) * mm, "end": v(-38.1, -82.55) * mm});
            skLineSegment(sketch, "E113", {"start": v(-63.5, -57.15) * mm, "end": v(-63.5, -39.69) * mm});
            skLineSegment(sketch, "E114", {"start": v(-71.44, -31.75) * mm, "end": v(-72.91, -31.75) * mm});
            skLineSegment(sketch, "E115", {"start": v(-78.52, -34.07) * mm, "end": v(-85.18, -40.73) * mm});
            skPoint(sketch, "E116.visualSharp", {"position": v(-76.2, -31.75) * mm});
            skArc(sketch, "E116.filletArc", {"start": v(-72.91, -31.75) * mm, "mid": v(-75.95, -32.35) * mm, "end": v(-78.52, -34.07) * mm});
            skPoint(sketch, "E117.visualSharp", {"position": v(-63.5, -31.75) * mm});
            skArc(sketch, "E117.filletArc", {"start": v(-63.5, -39.69) * mm, "mid": v(-65.82, -34.07) * mm, "end": v(-71.44, -31.75) * mm});
            skPoint(sketch, "E118.visualSharp", {"position": v(-63.5, -82.55) * mm});
            skArc(sketch, "E118.filletArc", {"start": v(-63.5, -57.15) * mm, "mid": v(-56.06, -75.11) * mm, "end": v(-38.1, -82.55) * mm});
            skPoint(sketch, "E119.visualSharp", {"position": v(0, -82.55) * mm});
            skArc(sketch, "E119.filletArc", {"start": v(-25.4, -82.55) * mm, "mid": v(-7.44, -75.11) * mm, "end": v(0, -57.15) * mm});
            skSolve(sketch);
        }
        {
            var Q0;
            Q0=sQuery(id+"F50.wireOp",VERTEX,"E115.end");
            var Q1;
            Q1=sQuery(id+"F50.wireOp",EDGE,"E115");
            cPlane(context, id + "F51", {"entities" : qUnion([Q0, Q1]), "cplaneType" : CPlaneType.LINE_POINT, "offset" : 25.4 * mm, "width" : 152.4 * mm, "height" : 152.4 * mm});
        }
        {
            var Q0;
            Q0=qCreatedBy(id+"F51.planeOp",FACE);
            var sketch = newSketch(context, id + "F52", { "sketchPlane" : qUnion([Q0])});
            skCircle(sketch, "E120", {"center": v(0, 31.43) * mm, "radius": 4.76 * mm});
            skSolve(sketch);
        }
        {
            var Q0;
            Q0 = qSketchRegion(id + "F52", true);
            var Q1;
            Q1=sQuery(id+"F50.wireOp",EDGE,"E115");
            var Q2;
            Q2=sQuery(id+"F50.wireOp",EDGE,"E116.filletArc");
            var Q3;
            Q3=sQuery(id+"F50.wireOp",EDGE,"E114");
            var Q4;
            Q4=sQuery(id+"F50.wireOp",EDGE,"E117.filletArc");
            var Q5;
            Q5=sQuery(id+"F50.wireOp",EDGE,"E113");
            var Q6;
            Q6=sQuery(id+"F50.wireOp",EDGE,"E118.filletArc");
            var Q7;
            Q7=sQuery(id+"F50.wireOp",EDGE,"E112");
            var Q8;
            Q8=sQuery(id+"F50.wireOp",EDGE,"E119.filletArc");
            var Q9;
            Q9=sQuery(id+"F50.wireOp",EDGE,"E111");
            var Q10;
            Q10=sQuery(id+"F42.wireOp",EDGE,"E87");
            var Q11;
            Q11=sQuery(id+"F42.wireOp",EDGE,"E89.filletArc");
            var Q12;
            Q12=sQuery(id+"F42.wireOp",EDGE,"E86");
            var Q13;
            Q13=sQuery(id+"F42.wireOp",EDGE,"E90.filletArc");
            var Q14;
            Q14=sQuery(id+"F42.wireOp",EDGE,"E88");
            var Q15;
            Q15=sQuery(id+"F49.wireOp",EDGE,"E102");
            var Q16;
            Q16=sQuery(id+"F49.wireOp",EDGE,"E110.filletArc");
            var Q17;
            Q17=sQuery(id+"F49.wireOp",EDGE,"E103");
            var Q18;
            Q18=sQuery(id+"F49.wireOp",EDGE,"E109.filletArc");
            var Q19;
            Q19=sQuery(id+"F49.wireOp",EDGE,"E104");
            var Q20;
            Q20=sQuery(id+"F49.wireOp",EDGE,"E108.filletArc");
            var Q21;
            Q21=sQuery(id+"F49.wireOp",EDGE,"E105");
            var Q22;
            Q22=sQuery(id+"F49.wireOp",EDGE,"E107.filletArc");
            var Q23;
            Q23=sQuery(id+"F49.wireOp",EDGE,"E106");
            sweep(context, id + "F53", {"profiles" : qUnion([Q0]), "path" : qUnion([Q1, Q2, Q3, Q4, Q5, Q6, Q7, Q8, Q9, Q10, Q11, Q12, Q13, Q14, Q15, Q16, Q17, Q18, Q19, Q20, Q21, Q22, Q23])});
        }
        {
            var Q0;
            Q0=qCreatedBy(id+"F44.planeOp",FACE);
            var sketch = newSketch(context, id + "F54", { "sketchPlane" : qUnion([Q0])});
            skCircle(sketch, "E121", {"center": v(-28.9, -50.8) * mm, "radius": 24.13 * mm});
            skCircle(sketch, "E122", {"center": v(-28.9, -50.8) * mm, "radius": 20.45 * mm});
            skSolve(sketch);
        }
        {
            var Q0;
            Q0 = qSketchRegion(id + "F54", true);
            extrude(context, id + "F55", {"entities" : qUnion([Q0]), "depth" : 12.7 * mm, "offsetDistance" : 25.4 * mm, "hasSecondDirection" : true, "secondDirectionOppositeDirection" : true, "secondDirectionDepth" : 127 * mm});
        }
        {
            var Q0;
            Q0=qCreatedBy(makeId("Front.planeOp"),FACE);
            var sketch = newSketch(context, id + "F56", { "sketchPlane" : qUnion([Q0])});
            skLineSegment(sketch, "E123.bottom", {"start": v(101.6, -4.76) * mm, "end": v(12.7, -4.76) * mm});
            skLineSegment(sketch, "E123.top", {"start": v(109.54, -68.26) * mm, "end": v(4.76, -68.26) * mm});
            skLineSegment(sketch, "E123.left", {"start": v(109.54, -12.7) * mm, "end": v(109.54, -68.26) * mm});
            skLineSegment(sketch, "E123.right", {"start": v(4.76, -12.7) * mm, "end": v(4.76, -68.26) * mm});
            skPoint(sketch, "E124.visualSharp", {"position": v(109.54, -4.76) * mm});
            skArc(sketch, "E124.filletArc", {"start": v(109.54, -12.7) * mm, "mid": v(107.21, -7.09) * mm, "end": v(101.6, -4.76) * mm});
            skPoint(sketch, "E125.visualSharp", {"position": v(4.76, -4.76) * mm});
            skArc(sketch, "E125.filletArc", {"start": v(12.7, -4.76) * mm, "mid": v(7.09, -7.09) * mm, "end": v(4.76, -12.7) * mm});
            skSolve(sketch);
        }
        {
            var Q0;
            Q0 = qSketchRegion(id + "F56", true);
            extrude(context, id + "F57", {"entities" : qUnion([Q0]), "depth" : 4.76 * mm, "offsetDistance" : 25.4 * mm, "hasSecondDirection" : true, "secondDirectionOppositeDirection" : true, "secondDirectionDepth" : 4.76 * mm});
        }
        {
            var Q0;
            Q0=sQuery(id+"F43.wireOp",VERTEX,"E92.start");
            var Q1;
            Q1=sQuery(id+"F45.wireOp",VERTEX,"E98.start");
            var Q2;
            Q2=sQuery(id+"F42.wireOp",VERTEX,"E88.end");
            cPlane(context, id + "F58", {"entities" : qUnion([Q0, Q1, Q2]), "cplaneType" : CPlaneType.THREE_POINT, "offset" : 25.4 * mm, "width" : 152.4 * mm, "height" : 152.4 * mm});
        }
        {
            var Q0;
            Q0=makeQuery(id+"F57.opExtrude","CAP_FACE",FACE,{"disambiguationData":[OSD([sQuery(id+"F56.wireOp",EDGE,"E123.bottom"),sQuery(id+"F56.wireOp",EDGE,"E123.top"),sQuery(id+"F56.wireOp",EDGE,"E123.left"),sQuery(id+"F56.wireOp",EDGE,"E123.right"),sQuery(id+"F56.wireOp",EDGE,"E124.filletArc"),sQuery(id+"F56.wireOp",EDGE,"E125.filletArc")])],"isStart":true});
            var sketch = newSketch(context, id + "F59", { "sketchPlane" : qUnion([Q0])});
            skLineSegment(sketch, "E126.bottom", {"start": v(-109.54, -68.26) * mm, "end": v(-90.49, -68.26) * mm});
            skLineSegment(sketch, "E126.top", {"start": v(-109.54, -23.81) * mm, "end": v(-98.43, -23.81) * mm});
            skLineSegment(sketch, "E126.left", {"start": v(-109.54, -68.26) * mm, "end": v(-109.54, -23.81) * mm});
            skLineSegment(sketch, "E126.right", {"start": v(-90.49, -68.26) * mm, "end": v(-90.49, -31.75) * mm});
            skLineSegment(sketch, "E127.bottom", {"start": v(-4.76, -68.26) * mm, "end": v(-23.81, -68.26) * mm});
            skLineSegment(sketch, "E127.top", {"start": v(-4.76, -23.81) * mm, "end": v(-15.88, -23.81) * mm});
            skLineSegment(sketch, "E127.left", {"start": v(-4.76, -68.26) * mm, "end": v(-4.76, -23.81) * mm});
            skLineSegment(sketch, "E127.right", {"start": v(-23.81, -68.26) * mm, "end": v(-23.81, -31.75) * mm});
            skPoint(sketch, "E128.visualSharp", {"position": v(-90.49, -23.81) * mm});
            skArc(sketch, "E128.filletArc", {"start": v(-90.49, -31.75) * mm, "mid": v(-92.81, -26.14) * mm, "end": v(-98.43, -23.81) * mm});
            skPoint(sketch, "E129.visualSharp", {"position": v(-23.81, -23.81) * mm});
            skArc(sketch, "E129.filletArc", {"start": v(-15.88, -23.81) * mm, "mid": v(-21.49, -26.14) * mm, "end": v(-23.81, -31.75) * mm});
            skCircle(sketch, "E130", {"center": v(-77.79, -50.8) * mm, "radius": 3.18 * mm});
            skCircle(sketch, "E131", {"center": v(-36.51, -50.8) * mm, "radius": 3.18 * mm});
            skSolve(sketch);
        }
        {
            var Q0;
            Q0 = qSketchRegion(id + "F59", true);
            extrude(context, id + "F60", {"entities" : qUnion([Q0]), "operationType" : NewBodyOperationType.REMOVE, "oppositeDirection" : true, "depth" : 25.4 * mm, "offsetDistance" : 25.4 * mm});
        }
        {
            var Q0;
            Q0=qCreatedBy(makeId("Top.planeOp"),FACE);
            var sketch = newSketch(context, id + "F61", { "sketchPlane" : qUnion([Q0])});
            skLineSegment(sketch, "E132.bottom", {"start": v(-50.8, 50.8) * mm, "end": v(0, 50.8) * mm});
            skLineSegment(sketch, "E132.top", {"start": v(-50.8, 0) * mm, "end": v(0, 0) * mm});
            skLineSegment(sketch, "E132.left", {"start": v(-50.8, 50.8) * mm, "end": v(-50.8, 0) * mm});
            skLineSegment(sketch, "E132.right", {"start": v(0, 50.8) * mm, "end": v(0, 0) * mm});
            skLineSegment(sketch, "E133.bottom", {"start": v(-44.45, 3.18) * mm, "end": v(-6.35, 3.18) * mm});
            skLineSegment(sketch, "E133.top", {"start": v(-44.45, 47.63) * mm, "end": v(-6.35, 47.63) * mm});
            skLineSegment(sketch, "E133.left", {"start": v(-47.63, 6.35) * mm, "end": v(-47.63, 44.45) * mm});
            skLineSegment(sketch, "E133.right", {"start": v(-3.18, 6.35) * mm, "end": v(-3.18, 44.45) * mm});
            skPoint(sketch, "E134.visualSharp", {"position": v(-47.63, 47.63) * mm});
            skArc(sketch, "E134.filletArc", {"start": v(-44.45, 47.63) * mm, "mid": v(-46.7, 46.7) * mm, "end": v(-47.63, 44.45) * mm});
            skPoint(sketch, "E135.visualSharp", {"position": v(-3.18, 47.63) * mm});
            skArc(sketch, "E135.filletArc", {"start": v(-3.18, 44.45) * mm, "mid": v(-4.1, 46.7) * mm, "end": v(-6.35, 47.63) * mm});
            skPoint(sketch, "E136.visualSharp", {"position": v(-3.18, 3.18) * mm});
            skArc(sketch, "E136.filletArc", {"start": v(-6.35, 3.18) * mm, "mid": v(-4.1, 4.1) * mm, "end": v(-3.18, 6.35) * mm});
            skPoint(sketch, "E137.visualSharp", {"position": v(-47.63, 3.18) * mm});
            skArc(sketch, "E137.filletArc", {"start": v(-47.63, 6.35) * mm, "mid": v(-46.7, 4.1) * mm, "end": v(-44.45, 3.17) * mm});
            skSolve(sketch);
        }
        {
            var Q0;
            Q0 = qSketchRegion(id + "F61", true);
            extrude(context, id + "F62", {"entities" : qUnion([Q0]), "depth" : 1270 * mm, "offsetDistance" : 25.4 * mm});
        }
    });
